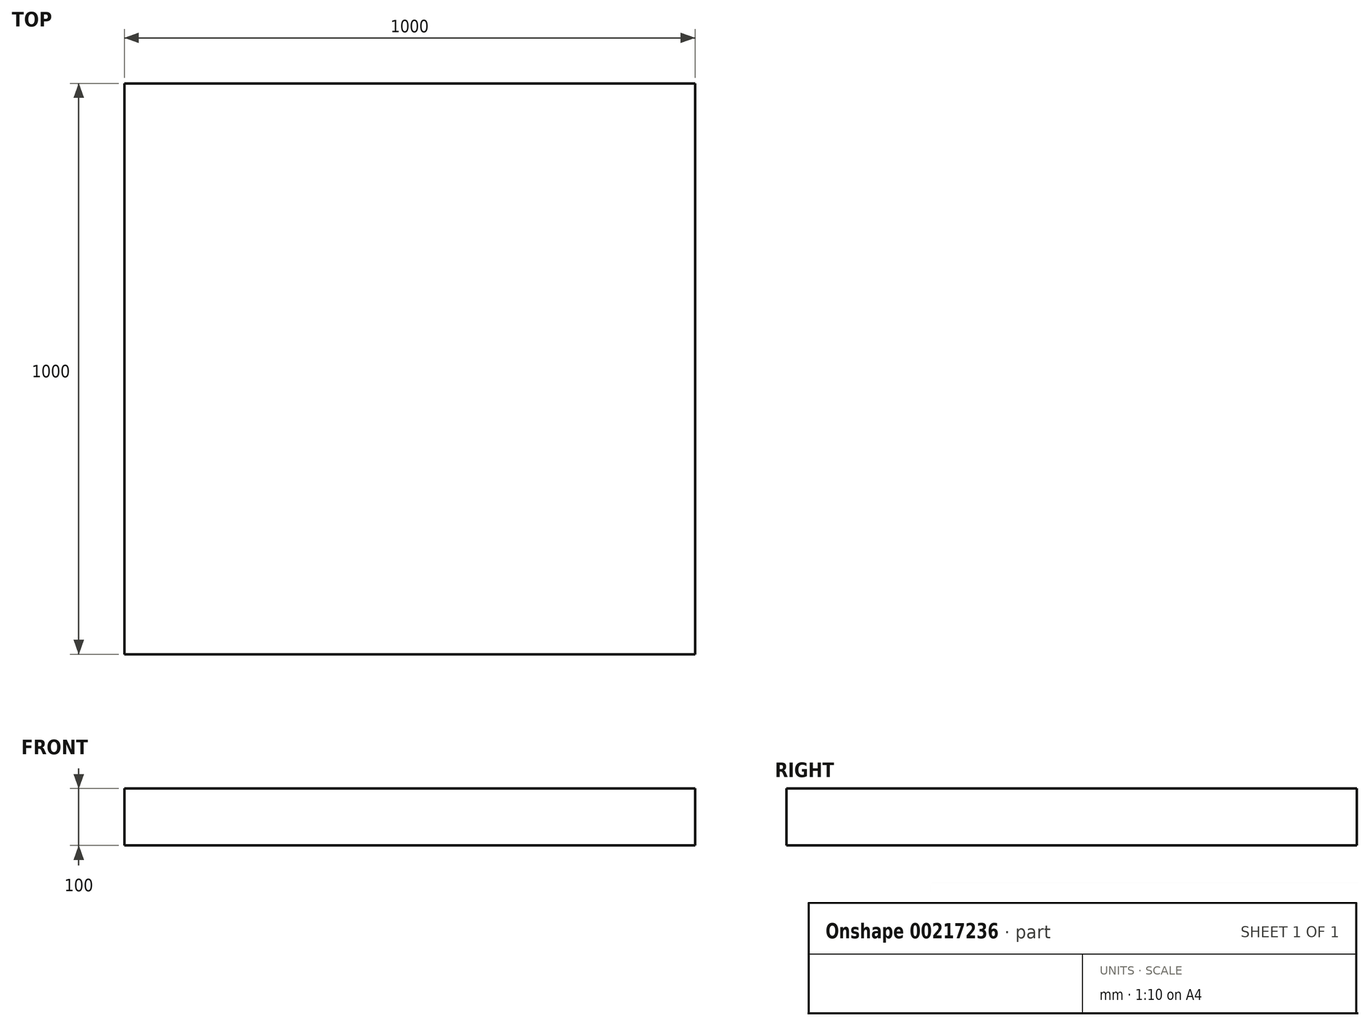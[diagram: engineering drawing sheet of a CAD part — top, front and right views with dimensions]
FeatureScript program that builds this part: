
annotation { "Feature Type Name" : "Feature", "Feature Type Description" : "" }
export const myFeature = defineFeature(function(context is Context, id is Id, definition is map)
    precondition{}
    {
        {
            var Q0;
            Q0=qCreatedBy(makeId("Top.planeOp"),FACE);
            var sketch = newSketch(context, id + "F0", { "sketchPlane" : qUnion([Q0])});
            skLineSegment(sketch, "E0.bottom", {"start": v(-500.44, 633.55) * mm, "end": v(499.56, 633.55) * mm});
            skLineSegment(sketch, "E0.top", {"start": v(-500.44, -366.45) * mm, "end": v(499.56, -366.45) * mm});
            skLineSegment(sketch, "E0.left", {"start": v(-500.44, 633.55) * mm, "end": v(-500.44, -366.45) * mm});
            skLineSegment(sketch, "E0.right", {"start": v(499.56, 633.55) * mm, "end": v(499.56, -366.45) * mm});
            skSolve(sketch);
        }
        {
            var Q0;
            Q0=makeQuery(id+"F0.imprint","IMPRINT",FACE,{"disambiguationData":[TD([[makeQuery(id+"F0.imprint","IMPRINT",EDGE,{"derivedFrom":sQuery(id+"F0.wireOp",EDGE,"E0.bottom")}),-1.0]])]});
            extrude(context, id + "F1", {"entities" : qUnion([Q0]), "depth" : 100 * mm});
        }
        {
            var Q0;
            Q0=qCreatedBy(makeId("Top.planeOp"),FACE);
            var sketch = newSketch(context, id + "F2", { "sketchPlane" : qUnion([Q0])});
            skCircle(sketch, "E1.cCircle", {"center": v(0, 138.33) * mm, "radius": 160.66 * mm, "construction": true});
            skLineSegment(sketch, "E1.0", {"start": v(-66.55, 298.99) * mm, "end": v(66.55, 298.99) * mm});
            skLineSegment(sketch, "E1.1", {"start": v(66.55, 298.99) * mm, "end": v(160.66, 204.88) * mm});
            skLineSegment(sketch, "E1.2", {"start": v(160.66, 204.88) * mm, "end": v(160.66, 71.79) * mm});
            skLineSegment(sketch, "E1.3", {"start": v(160.66, 71.79) * mm, "end": v(66.55, -22.32) * mm});
            skLineSegment(sketch, "E1.4", {"start": v(66.55, -22.32) * mm, "end": v(-66.55, -22.32) * mm});
            skLineSegment(sketch, "E1.5", {"start": v(-66.55, -22.32) * mm, "end": v(-160.66, 71.79) * mm});
            skLineSegment(sketch, "E1.6", {"start": v(-160.66, 71.79) * mm, "end": v(-160.66, 204.88) * mm});
            skLineSegment(sketch, "E1.7", {"start": v(-160.66, 204.88) * mm, "end": v(-66.55, 298.99) * mm});
            skPoint(sketch, "E1.0.midPoint", {"position": v(0, 298.99) * mm});
            skSolve(sketch);
        }
        {
            var Q0;
            Q0=makeQuery(id+"F2.imprint","IMPRINT",FACE,{"disambiguationData":[TD([[makeQuery(id+"F2.imprint","IMPRINT",EDGE,{"derivedFrom":sQuery(id+"F2.wireOp",EDGE,"E1.0")}),-1.0]])]});
            var Q1;
            Q1=sQuery(id+"F2.wireOp",EDGE,"E1.0");
            var Q2;
            Q2=sQuery(id+"F2.wireOp",EDGE,"E1.7");
            var Q3;
            Q3=sQuery(id+"F2.wireOp",EDGE,"E1.6");
            var Q4;
            Q4=sQuery(id+"F2.wireOp",EDGE,"E1.5");
            var Q5;
            Q5=sQuery(id+"F2.wireOp",EDGE,"E1.4");
            var Q6;
            Q6=sQuery(id+"F2.wireOp",EDGE,"E1.3");
            var Q7;
            Q7=sQuery(id+"F2.wireOp",EDGE,"E1.2");
            var Q8;
            Q8=sQuery(id+"F2.wireOp",EDGE,"E1.1");
            extrude(context, id + "F3", {"entities" : qUnion([Q0]), "bodyType" : ToolBodyType.SURFACE, "surfaceEntities" : qUnion([Q1, Q2, Q3, Q4, Q5, Q6, Q7, Q8]), "depth" : 80 * mm});
        }
        {
            var Q0;
            Q0 = qSketchRegion(id + "F2", true);
            extrude(context, id + "F4", {"entities" : qUnion([Q0]), "operationType" : NewBodyOperationType.REMOVE, "depth" : 80 * mm});
        }
        {
            var Q0;
            Q0=makeQuery(id+"F4.boolean.opBoolean","COPY",FACE,{"derivedFrom":makeQuery(id+"F4.opExtrude","CAP_FACE",FACE,{"disambiguationData":[OSD([sQuery(id+"F2.wireOp",EDGE,"E1.0"),sQuery(id+"F2.wireOp",EDGE,"E1.1"),sQuery(id+"F2.wireOp",EDGE,"E1.2"),sQuery(id+"F2.wireOp",EDGE,"E1.3"),sQuery(id+"F2.wireOp",EDGE,"E1.4"),sQuery(id+"F2.wireOp",EDGE,"E1.5"),sQuery(id+"F2.wireOp",EDGE,"E1.6"),sQuery(id+"F2.wireOp",EDGE,"E1.7")])],"isStart":false})});
            extrude(context, id + "F5", {"entities" : qUnion([Q0]), "operationType" : NewBodyOperationType.ADD, "depth" : 80 * mm});
        }
    });
